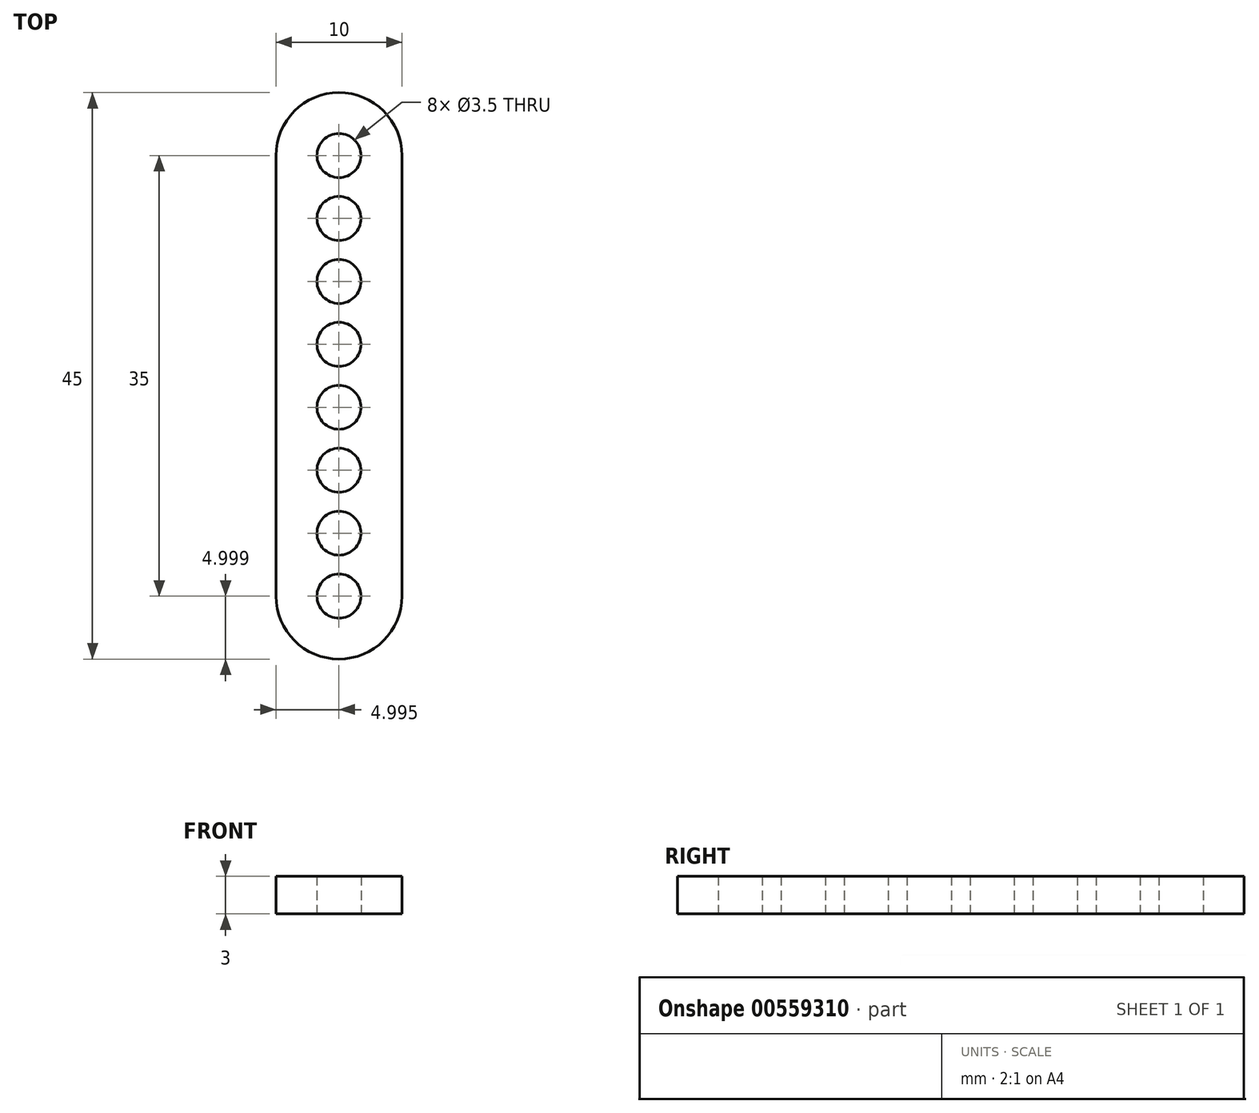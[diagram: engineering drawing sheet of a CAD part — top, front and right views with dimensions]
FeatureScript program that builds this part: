
annotation { "Feature Type Name" : "Feature", "Feature Type Description" : "" }
export const myFeature = defineFeature(function(context is Context, id is Id, definition is map)
    precondition{}
    {
        {
            var Q0;
            Q0=qCreatedBy(makeId("Top.planeOp"),FACE);
            var sketch = newSketch(context, id + "F0", { "sketchPlane" : qUnion([Q0])});
            skLineSegment(sketch, "E0", {"start": v(-21.26, 15.74) * mm, "end": v(-21.26, 20.74) * mm});
            skLineSegment(sketch, "E1", {"start": v(-21.26, -9.26) * mm, "end": v(-21.26, -14.26) * mm});
            skCircle(sketch, "E2", {"center": v(-21.26, 15.74) * mm, "radius": 1.75 * mm});
            skCircle(sketch, "E3", {"center": v(-21.26, 20.74) * mm, "radius": 1.75 * mm});
            skCircle(sketch, "E4", {"center": v(-21.26, -9.26) * mm, "radius": 1.75 * mm});
            skCircle(sketch, "E5", {"center": v(-21.26, -14.26) * mm, "radius": 1.75 * mm});
            skLineSegment(sketch, "E6", {"start": v(-21.26, 20.74) * mm, "end": v(-16.26, 20.74) * mm});
            skLineSegment(sketch, "E7", {"start": v(-21.26, -14.26) * mm, "end": v(-21.26, -19.26) * mm});
            skLineSegment(sketch, "E8", {"start": v(-21.26, 3.24) * mm, "end": v(-26.26, 3.24) * mm});
            skLineSegment(sketch, "E9", {"start": v(-16.26, -19.26) * mm, "end": v(-26.26, -19.26) * mm});
            skLineSegment(sketch, "E10", {"start": v(-26.26, -19.26) * mm, "end": v(-26.26, 25.74) * mm});
            skLineSegment(sketch, "E11", {"start": v(-26.26, 25.74) * mm, "end": v(-16.26, 25.74) * mm});
            skLineSegment(sketch, "E12", {"start": v(-16.26, 25.74) * mm, "end": v(-16.26, -19.26) * mm});
            skLineSegment(sketch, "E13", {"start": v(-21.26, 15.74) * mm, "end": v(-21.26, 10.74) * mm, "construction": true});
            skLineSegment(sketch, "E14", {"start": v(-21.26, 10.74) * mm, "end": v(-21.26, 5.74) * mm, "construction": true});
            skLineSegment(sketch, "E15", {"start": v(-21.26, 5.74) * mm, "end": v(-21.26, 0.74) * mm, "construction": true});
            skLineSegment(sketch, "E16", {"start": v(-21.26, 0.74) * mm, "end": v(-21.26, -4.26) * mm, "construction": true});
            skLineSegment(sketch, "E17", {"start": v(-21.26, -4.26) * mm, "end": v(-21.26, -9.26) * mm, "construction": true});
            skCircle(sketch, "E18", {"center": v(-21.26, 10.74) * mm, "radius": 1.75 * mm});
            skCircle(sketch, "E19", {"center": v(-21.26, 5.74) * mm, "radius": 1.75 * mm});
            skCircle(sketch, "E20", {"center": v(-21.26, 0.74) * mm, "radius": 1.75 * mm});
            skCircle(sketch, "E21", {"center": v(-21.26, -4.26) * mm, "radius": 1.75 * mm});
            skSolve(sketch);
        }
        {
            var Q0;
            Q0 = qSketchRegion(id + "F0", true);
            extrude(context, id + "F1", {"entities" : qUnion([Q0]), "depth" : 3 * mm, "offsetDistance" : 25 * mm});
        }
        {
            var Q0;
            Q0=makeQuery(id+"F1.opExtrude","SWEPT_EDGE",EDGE,{"disambiguationData":[OSD([sQuery(id+"F0.wireOp",EDGE,"E11"),sQuery(id+"F0.wireOp",EDGE,"E12")])]});
            var Q1;
            Q1=makeQuery(id+"F1.opExtrude","SWEPT_EDGE",EDGE,{"disambiguationData":[OSD([sQuery(id+"F0.wireOp",EDGE,"E10"),sQuery(id+"F0.wireOp",EDGE,"E11")])]});
            var Q2;
            Q2=makeQuery(id+"F1.opExtrude","SWEPT_EDGE",EDGE,{"disambiguationData":[OSD([sQuery(id+"F0.wireOp",EDGE,"E9"),sQuery(id+"F0.wireOp",EDGE,"E12")])]});
            var Q3;
            Q3=makeQuery(id+"F1.opExtrude","SWEPT_EDGE",EDGE,{"disambiguationData":[OSD([sQuery(id+"F0.wireOp",EDGE,"E9"),sQuery(id+"F0.wireOp",EDGE,"E10")])]});
            fillet(context, id + "F2", {"entities" : qUnion([Q0, Q1, Q2, Q3]), "tangentPropagation" : true, "radius" : 5 * mm, "defaultsChanged" : false, "vertexSettings" : [], "allowEdgeOverflow" : false});
        }
    });
